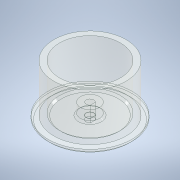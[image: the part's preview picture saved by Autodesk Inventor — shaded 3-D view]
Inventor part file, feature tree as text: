
AUTODESK INVENTOR PART (.ipt)
format: ipt  version: 2020 (Build 240168000, 168)  size: 163,328 bytes
history: native  units: mm
features: extrude x4, sketch x4, chamfer x2, plane x1
ambient origin geometry x8: Origin, YZ Plane, XZ Plane, XY Plane, X Axis, Y Axis, Z Axis, Center Point
bodies: Solid1 (feature_tree)
feature tree (11):
  extrude  "Extrusion1"  Depth=3.0mm
  extrude  "Extrusion2"  Depth=25.0mm
  plane  "Work Plane1"
  extrude  "Extrusion3"  Depth=2.0mm
  extrude  "Extrusion4"  Depth=0.5mm
  chamfer  "Chamfer1"  Distance=1.625mm
  chamfer  "Chamfer2"  Distance=28.0mm
  sketch  "Sketch1"  dims[d0=38.0mm d1=3.0mm]
  sketch  "Sketch2"  dims[d2=25.0mm d3=0.0mm d4=3.0mm]
  sketch  "Sketch3"  dims[d5=2.0mm d6=0.0mm d8=4.25mm]
  sketch  "Sketch4"  dims[d9=9.0mm d10=4.5mm d11=1.625mm d12=28.0mm d13=0.0mm d14=3.0mm d15=4.0mm d16=6.0mm d17=0.0mm d21=1.0mm d22=2.0mm d23=45.0deg d24=1.0mm d25=2.0mm d26=45.0deg d18=0.5mm d19=0.872665mm d20=0.5mm]
